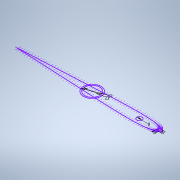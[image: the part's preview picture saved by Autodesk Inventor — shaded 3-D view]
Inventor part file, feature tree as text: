
AUTODESK INVENTOR PART (.ipt)
format: ipt  version: 2022 (Build 260153000, 153)  size: 129,024 bytes
history: native  units: mm
features: sketch x1
ambient origin geometry x8: Origin, YZ Plane, XZ Plane, XY Plane, X Axis, Y Axis, Z Axis, Center Point
feature tree (1):
  sketch  "Sketch1"  dims[d0=23.0mm d1=27.0mm d2=8.0mm d3=5.0mm d4=5.0mm]
